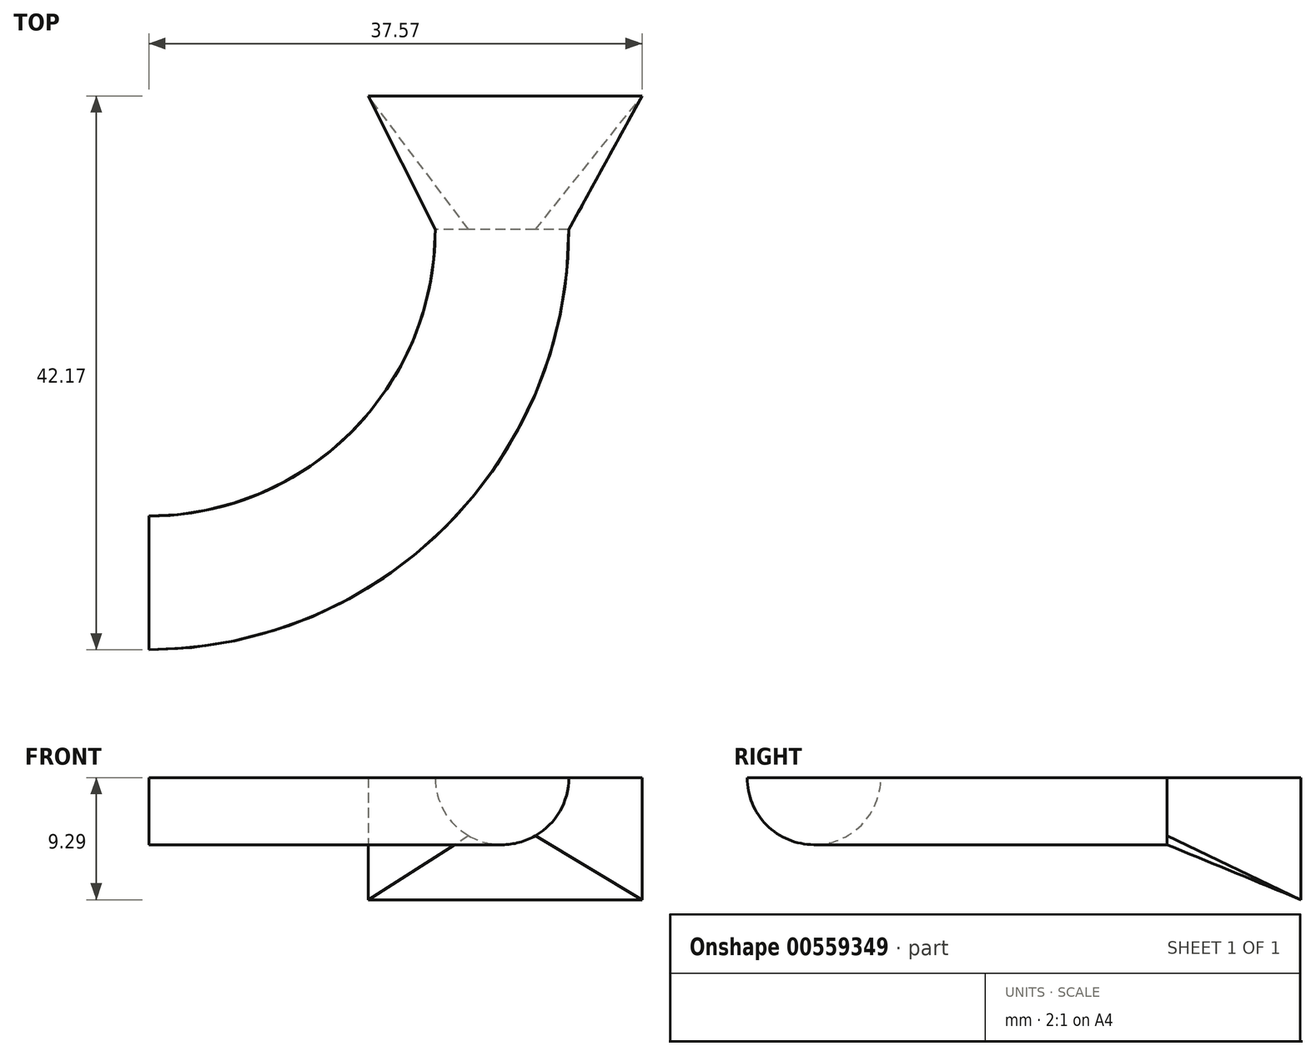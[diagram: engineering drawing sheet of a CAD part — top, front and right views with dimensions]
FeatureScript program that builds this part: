
annotation { "Feature Type Name" : "Feature", "Feature Type Description" : "" }
export const myFeature = defineFeature(function(context is Context, id is Id, definition is map)
    precondition{}
    {
        {
            var Q0;
            Q0=qCreatedBy(makeId("Top.planeOp"),FACE);
            var sketch = newSketch(context, id + "F0", { "sketchPlane" : qUnion([Q0])});
            skArc(sketch, "E0", {"start": v(0, 0) * mm, "mid": v(19.02, 7.88) * mm, "end": v(26.9, 26.9) * mm});
            skSolve(sketch);
        }
        {
            var Q0;
            Q0=qCreatedBy(makeId("Right.planeOp"),FACE);
            var sketch = newSketch(context, id + "F1", { "sketchPlane" : qUnion([Q0])});
            skLineSegment(sketch, "E1", {"start": v(0, 0) * mm, "end": v(-5.09, 0) * mm});
            skLineSegment(sketch, "E2", {"start": v(0, 0) * mm, "end": v(5.09, 0) * mm});
            skArc(sketch, "E3", {"start": v(-5.09, 0) * mm, "mid": v(0, -5.1) * mm, "end": v(5.09, 0) * mm});
            skSolve(sketch);
        }
        {
            var Q0;
            Q0=makeQuery(id+"F1.imprint","IMPRINT",FACE,{"disambiguationData":[TD([[makeQuery(id+"F1.imprint","IMPRINT",EDGE,{"derivedFrom":sQuery(id+"F1.wireOp",EDGE,"E1")}),1.0]])]});
            var Q1;
            Q1=sQuery(id+"F0.wireOp",EDGE,"E0");
            sweep(context, id + "F2", {"profiles" : qUnion([Q0]), "path" : qUnion([Q1])});
        }
        {
            var Q0;
            Q0=qCreatedBy(makeId("Front.planeOp"),FACE);
            cPlane(context, id + "F3", {"entities" : qUnion([Q0]), "cplaneType" : CPlaneType.OFFSET, "offset" : 37.08 * mm, "oppositeDirection" : true, "width" : 152.4 * mm, "height" : 152.4 * mm});
        }
        {
            var Q0;
            Q0=qCreatedBy(id+"F3.planeOp",FACE);
            var sketch = newSketch(context, id + "F4", { "sketchPlane" : qUnion([Q0])});
            skLineSegment(sketch, "E4.bottom", {"start": v(37.57, 0) * mm, "end": v(16.72, 0) * mm});
            skLineSegment(sketch, "E4.top", {"start": v(37.57, -9.3) * mm, "end": v(16.72, -9.3) * mm});
            skLineSegment(sketch, "E4.left", {"start": v(37.57, 0) * mm, "end": v(37.57, -9.3) * mm});
            skLineSegment(sketch, "E4.right", {"start": v(16.72, 0) * mm, "end": v(16.72, -9.3) * mm});
            skSolve(sketch);
        }
        {
            var Q1;
            Q1=makeQuery(id+"F2.opSweep","CAP_FACE",FACE,{"disambiguationData":[OSD([sQuery(id+"F0.wireOp",VERTEX,"E0.end"),sQuery(id+"F1.wireOp",EDGE,"E1"),sQuery(id+"F1.wireOp",EDGE,"E2"),sQuery(id+"F1.wireOp",EDGE,"E3")])],"isStart":false});
            var Q2;
            Q2=makeQuery(id+"F4.imprint","IMPRINT",FACE,{"disambiguationData":[TD([[makeQuery(id+"F4.imprint","IMPRINT",EDGE,{"derivedFrom":sQuery(id+"F4.wireOp",EDGE,"E4.bottom")}),1.0]])]});
            loft(context, id + "F5", {"operationType" : NewBodyOperationType.ADD, "sheetProfilesArray" : [{ "sheetProfileEntities" : qUnion([Q1]) }, { "sheetProfileEntities" : qUnion([Q2]) }]});
        }
    });
